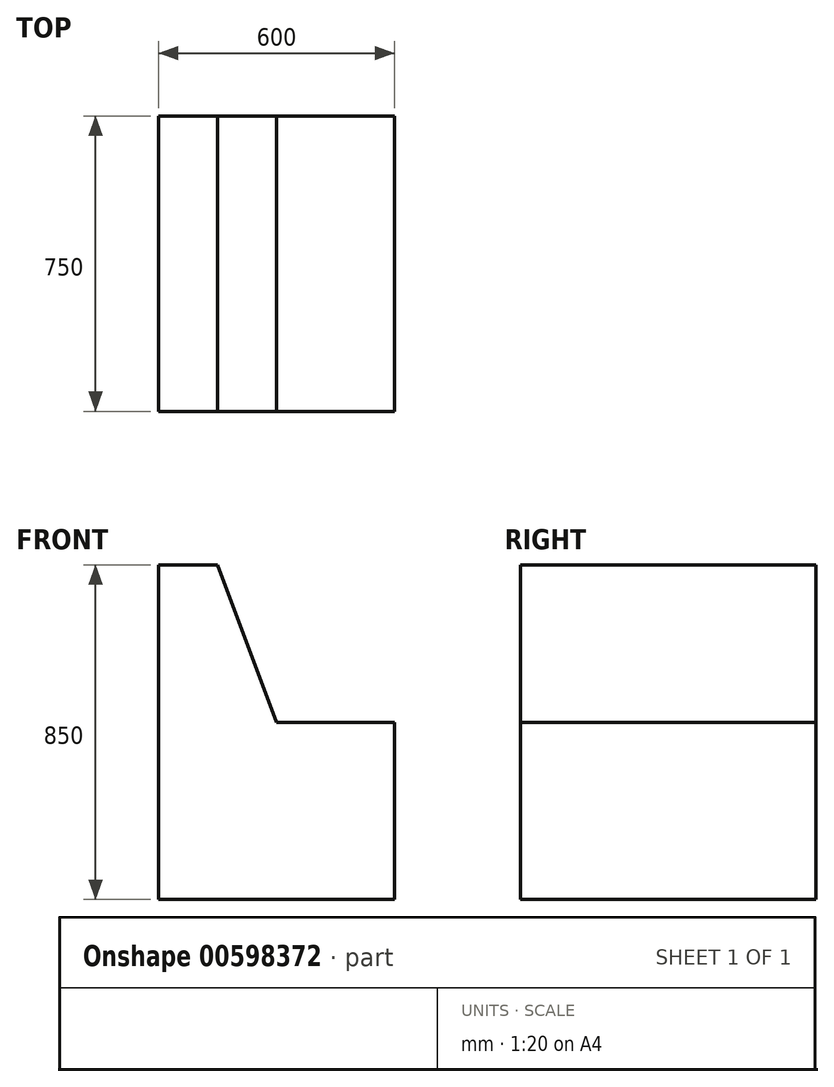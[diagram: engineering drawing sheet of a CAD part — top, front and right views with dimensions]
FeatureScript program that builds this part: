
annotation { "Feature Type Name" : "Feature", "Feature Type Description" : "" }
export const myFeature = defineFeature(function(context is Context, id is Id, definition is map)
    precondition{}
    {
        {
            var Q0;
            Q0=qCreatedBy(makeId("Front.planeOp"),FACE);
            var sketch = newSketch(context, id + "F0", { "sketchPlane" : qUnion([Q0])});
            skLineSegment(sketch, "E0.bottom", {"start": v(0, 0) * mm, "end": v(600, 0) * mm});
            skLineSegment(sketch, "E0.top", {"start": v(0, 450) * mm, "end": v(600, 450) * mm});
            skLineSegment(sketch, "E0.left", {"start": v(0, 0) * mm, "end": v(0, 450) * mm});
            skLineSegment(sketch, "E0.right", {"start": v(600, 0) * mm, "end": v(600, 450) * mm});
            skLineSegment(sketch, "E1", {"start": v(300, 450) * mm, "end": v(150, 850) * mm});
            skLineSegment(sketch, "E2", {"start": v(150, 850) * mm, "end": v(0, 850) * mm});
            skLineSegment(sketch, "E3", {"start": v(0, 850) * mm, "end": v(0, 450) * mm});
            skSolve(sketch);
        }
        {
            var Q0;
            Q0=makeQuery(id+"F0.imprint","IMPRINT",FACE,{"disambiguationData":[TD([[makeQuery(id+"F0.imprint","IMPRINT",EDGE,{"derivedFrom":sQuery(id+"F0.wireOp",EDGE,"E0.bottom")}),1.0]])]});
            var Q1;
            {var subQ2=sQuery(id+"F0.wireOp",EDGE,"E1");Q1=makeQuery(id+"F0.imprint","IMPRINT",FACE,{"disambiguationData":[TD([[makeQuery(id+"F0.imprint","IMPRINT",EDGE,{"derivedFrom":subQ2}),1.0]])]});}
            extrude(context, id + "F1", {"entities" : qUnion([Q0, Q1]), "depth" : 750 * mm, "offsetDistance" : 25 * mm});
        }
    });
